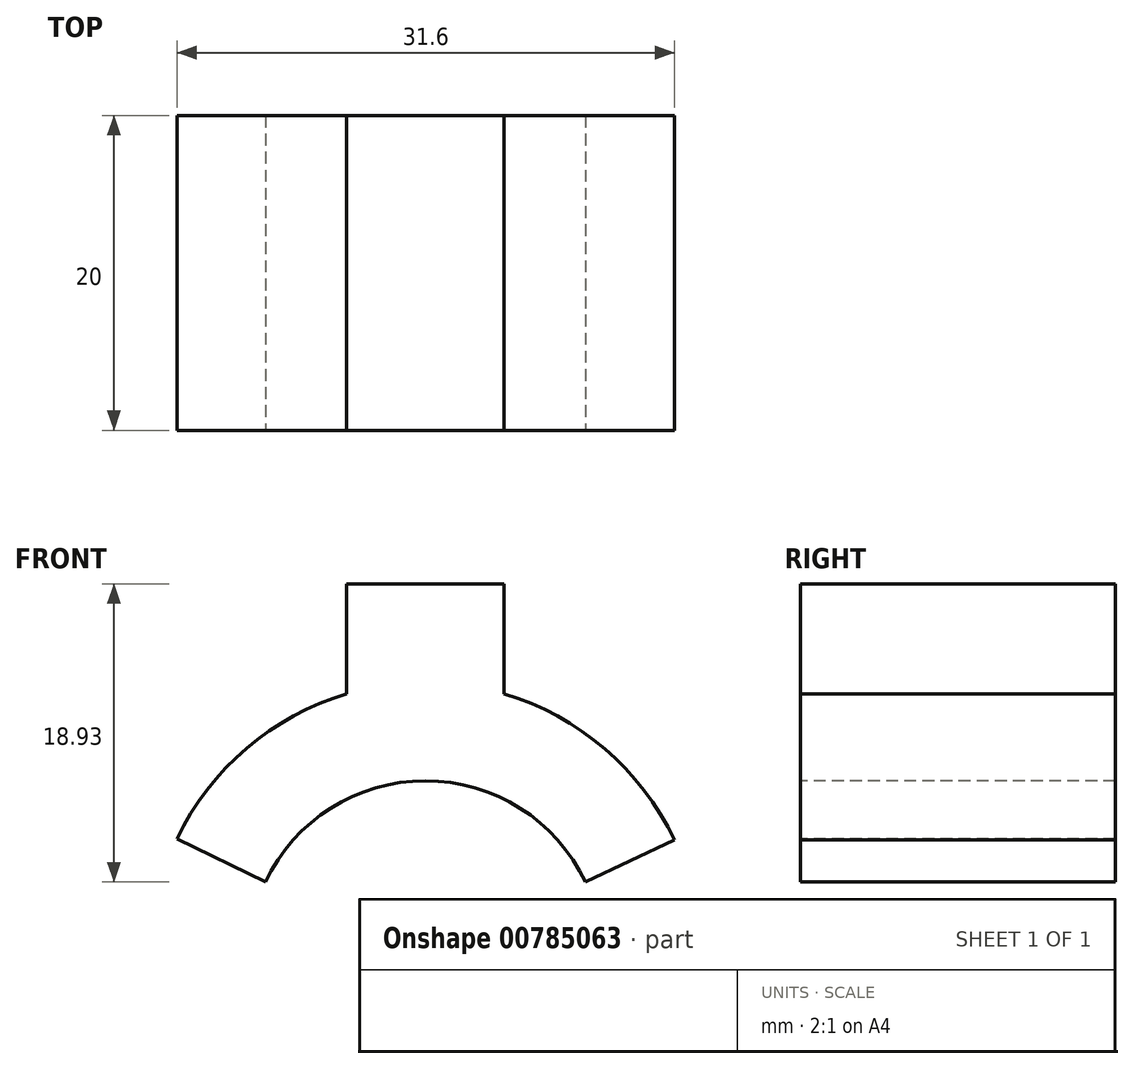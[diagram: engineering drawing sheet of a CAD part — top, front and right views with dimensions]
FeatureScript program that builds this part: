
annotation { "Feature Type Name" : "Feature", "Feature Type Description" : "" }
export const myFeature = defineFeature(function(context is Context, id is Id, definition is map)
    precondition{}
    {
        {
            var Q0;
            Q0=qCreatedBy(makeId("Front.planeOp"),FACE);
            var sketch = newSketch(context, id + "F0", { "sketchPlane" : qUnion([Q0])});
            skLineSegment(sketch, "E0", {"start": v(24.92, 23.9) * mm, "end": v(19.3, 26.63) * mm});
            skLineSegment(sketch, "E1", {"start": v(45.25, 23.9) * mm, "end": v(50.9, 26.58) * mm});
            skArc(sketch, "E2", {"start": v(50.9, 26.58) * mm, "mid": v(35.12, 36.58) * mm, "end": v(19.3, 26.63) * mm});
            skArc(sketch, "E3", {"start": v(24.92, 23.9) * mm, "mid": v(35.09, 30.33) * mm, "end": v(45.25, 23.9) * mm});
            skLineSegment(sketch, "E4", {"start": v(35.09, 30.33) * mm, "end": v(40.09, 30.33) * mm});
            skLineSegment(sketch, "E5", {"start": v(40.09, 30.33) * mm, "end": v(30.09, 30.33) * mm});
            skLineSegment(sketch, "E6.bottom", {"start": v(30.09, 30.33) * mm, "end": v(40.09, 30.33) * mm});
            skLineSegment(sketch, "E6.top", {"start": v(30.09, 42.83) * mm, "end": v(40.09, 42.83) * mm});
            skLineSegment(sketch, "E6.left", {"start": v(30.09, 30.33) * mm, "end": v(30.09, 42.83) * mm});
            skLineSegment(sketch, "E6.right", {"start": v(40.09, 30.33) * mm, "end": v(40.09, 42.83) * mm});
            skSolve(sketch);
        }
        {
            var Q0;
            Q0=makeQuery(id+"F0.imprint","IMPRINT",FACE,{"disambiguationData":[TD([[makeQuery(id+"F0.imprint","IMPRINT",EDGE,{"derivedFrom":sQuery(id+"F0.wireOp",EDGE,"E0")}),-1.0]])]});
            var Q1;
            {var subQ3=sQuery(id+"F0.wireOp",EDGE,"E2");var subQ6=sQuery(id+"F0.wireOp",EDGE,"E6.right");var subQ8=makeQuery(id+"F0.imprint","INTERSECT",VERTEX,{"derivedFrom":[subQ3,subQ6]});Q1=makeQuery(id+"F0.imprint","IMPRINT",FACE,{"disambiguationData":[TD([[makeQuery(id+"F0.imprint","IMPRINT",EDGE,{"disambiguationData":[TD([[subQ8,-1.0]])],"derivedFrom":subQ3}),1.0]])]});}
            var Q2;
            {var subQ5=sQuery(id+"F0.wireOp",EDGE,"E6.top");Q2=makeQuery(id+"F0.imprint","IMPRINT",FACE,{"disambiguationData":[TD([[makeQuery(id+"F0.imprint","IMPRINT",EDGE,{"derivedFrom":subQ5}),-1.0]])]});}
            var Q3;
            {var subQ6=sQuery(id+"F0.wireOp",EDGE,"E1");Q3=makeQuery(id+"F0.imprint","IMPRINT",FACE,{"disambiguationData":[TD([[makeQuery(id+"F0.imprint","IMPRINT",EDGE,{"derivedFrom":subQ6}),1.0]])]});}
            extrude(context, id + "F1", {"entities" : qUnion([Q0, Q1, Q2, Q3]), "oppositeDirection" : true, "depth" : 20 * mm, "offsetDistance" : 25 * mm});
        }
    });
